AUTODESK INVENTOR PART (.ipt)
format: ipt  version: 2016 (Build 200138000, 138)  size: 149,504 bytes
history: native  units: mm
features: sweep x1
ambient origin geometry x8: Origin, YZ Plane, XZ Plane, XY Plane, X Axis, Y Axis, Z Axis, Center Point
bodies: Solid1 (feature_tree)
feature tree (1):
  sweep  "Sweep1"
